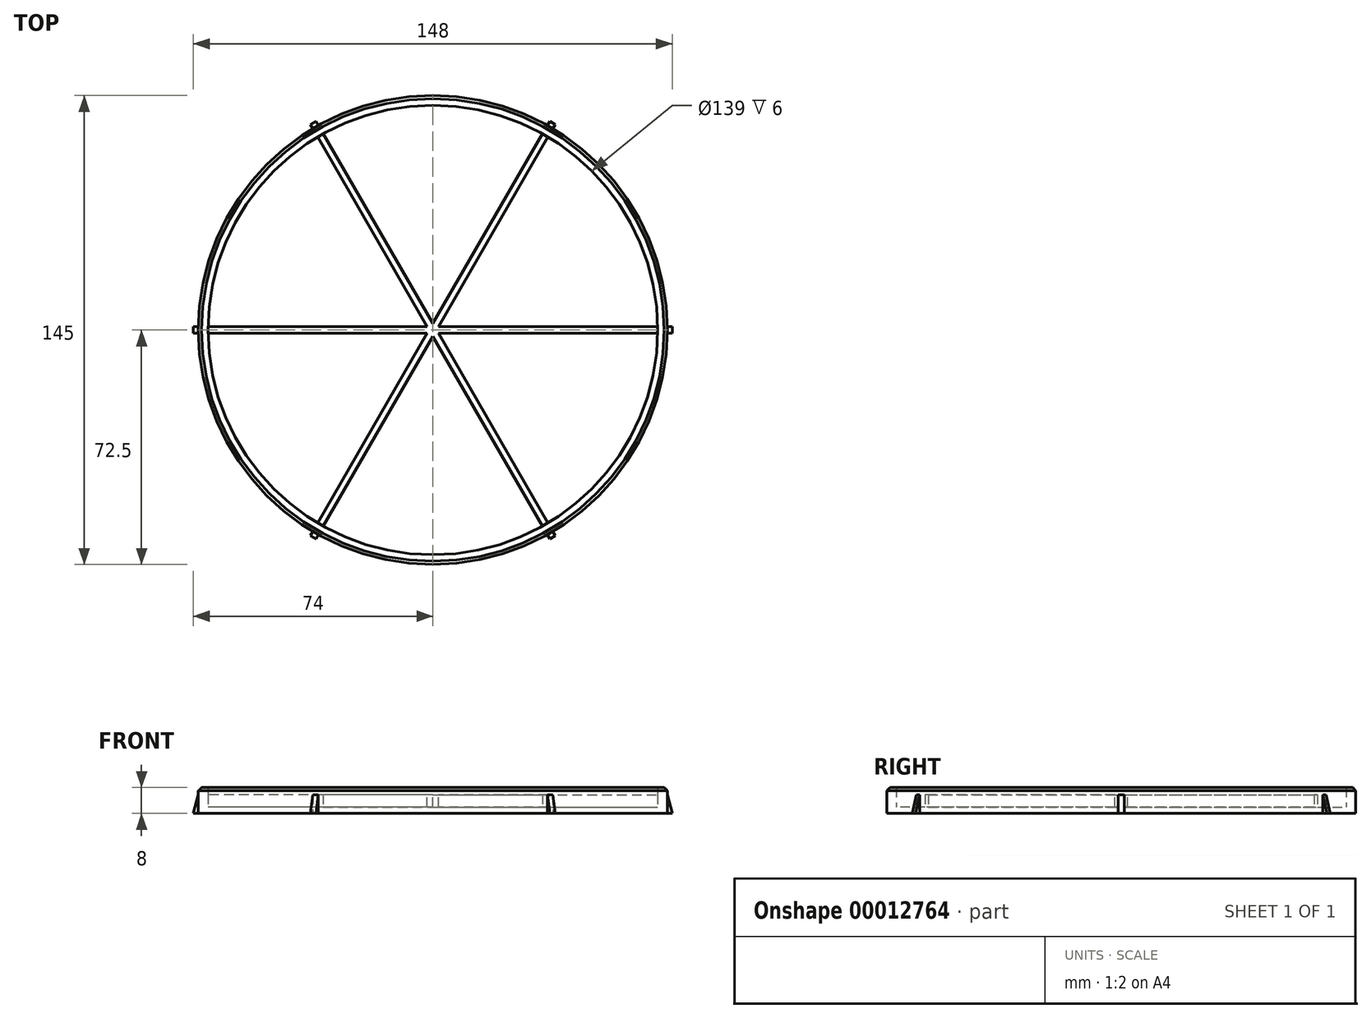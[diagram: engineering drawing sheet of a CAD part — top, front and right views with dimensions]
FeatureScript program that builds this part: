
annotation { "Feature Type Name" : "Feature", "Feature Type Description" : "" }
export const myFeature = defineFeature(function(context is Context, id is Id, definition is map)
    precondition{}
    {
        {
            var Q0;
            Q0=qCreatedBy(makeId("Top.planeOp"),FACE);
            var sketch = newSketch(context, id + "F0", { "sketchPlane" : qUnion([Q0])});
            skCircle(sketch, "E0", {"center": v(0, 0) * mm, "radius": 72.5 * mm});
            skSolve(sketch);
        }
        {
            var Q0;
            Q0 = qSketchRegion(id + "F0", true);
            extrude(context, id + "F1", {"entities" : qUnion([Q0]), "depth" : 2 * mm});
        }
        {
            var Q0;
            Q0=qCreatedBy(makeId("Front.planeOp"),FACE);
            var sketch = newSketch(context, id + "F2", { "sketchPlane" : qUnion([Q0])});
            skLineSegment(sketch, "E1.bottom", {"start": v(0, 0) * mm, "end": v(74, 0) * mm});
            skLineSegment(sketch, "E1.top", {"start": v(0, 5.8) * mm, "end": v(72.5, 5.8) * mm});
            skLineSegment(sketch, "E1.left", {"start": v(0, 0) * mm, "end": v(0, 5.8) * mm});
            skLineSegment(sketch, "E1.right", {"start": v(74, 0) * mm, "end": v(72.5, 5.8) * mm});
            skSolve(sketch);
        }
        {
            var Q0;
            Q0 = qSketchRegion(id + "F2", true);
            extrude(context, id + "F3", {"entities" : qUnion([Q0]), "operationType" : NewBodyOperationType.ADD, "endBound" : BoundingType.SYMMETRIC, "depth" : 2 * mm});
        }
        {
            var Q0;
            Q0=makeQuery(id+"F1.opExtrude","SWEPT_BODY",BODY,{"disambiguationData":[OSD([sQuery(id+"F0.wireOp",EDGE,"E0")])]});
            var Q1;
            Q1=makeQuery(id+"F1.opExtrude","CAP_EDGE",EDGE,{"disambiguationData":[OSD([sQuery(id+"F0.wireOp",EDGE,"E0")])],"isStart":false});
            circularPattern(context, id + "F4", {"operationType" : NewBodyOperationType.ADD, "entities" : qUnion([Q0]), "axis" : qUnion([Q1]), "angle" : 60 * degree, "instanceCount" : 6});
        }
        {
            var Q0;
            Q0=qCreatedBy(makeId("Front.planeOp"),FACE);
            var sketch = newSketch(context, id + "F5", { "sketchPlane" : qUnion([Q0])});
            skLineSegment(sketch, "E2.bottom", {"start": v(69.5, 0) * mm, "end": v(72.5, 0) * mm});
            skLineSegment(sketch, "E2.top", {"start": v(69.5, 8) * mm, "end": v(72.5, 8) * mm});
            skLineSegment(sketch, "E2.left", {"start": v(69.5, 0) * mm, "end": v(69.5, 8) * mm});
            skLineSegment(sketch, "E2.right", {"start": v(72.5, 0) * mm, "end": v(72.5, 8) * mm});
            skSolve(sketch);
        }
        {
            var Q0;
            Q0 = qSketchRegion(id + "F5", true);
            var Q1;
            {var subQ0=sQuery(id+"F0.wireOp",EDGE,"E0");var subQ1=sQuery(id+"F2.wireOp",EDGE,"E1.bottom");var subQ2=sQuery(id+"F2.wireOp",EDGE,"E1.top");var subQ3=sQuery(id+"F2.wireOp",EDGE,"E1.left");var subQ4=sQuery(id+"F2.wireOp",EDGE,"E1.right");var subQ5=makeQuery(id+"F3.opExtrude","CAP_FACE",FACE,{"disambiguationData":[OSD([subQ1,subQ2,subQ3,subQ4])],"isStart":false});Q1=makeQuery(id+"F4.boolean.opBoolean","SPLIT",EDGE,{"disambiguationData":[TD([subQ5])],"derivedFrom":makeQuery(id+"F1.opExtrude","CAP_EDGE",EDGE,{"disambiguationData":[OSD([subQ0])],"isStart":false})});}
            revolve(context, id + "F6", {"operationType" : NewBodyOperationType.ADD, "entities" : qUnion([Q0]), "axis" : qUnion([Q1]), "revolveType" : RevolveType.FULL});
        }
        {
            var Q0;
            Q0=makeQuery(id+"F6.opRevolve","SWEPT_EDGE",EDGE,{"disambiguationData":[OSD([sQuery(id+"F5.wireOp",EDGE,"E2.top"),sQuery(id+"F5.wireOp",EDGE,"E2.right")])]});
            chamfer(context, id + "F7", {"entities" : qUnion([Q0]), "width" : 1 * mm, "tangentPropagation" : true});
        }
    });
